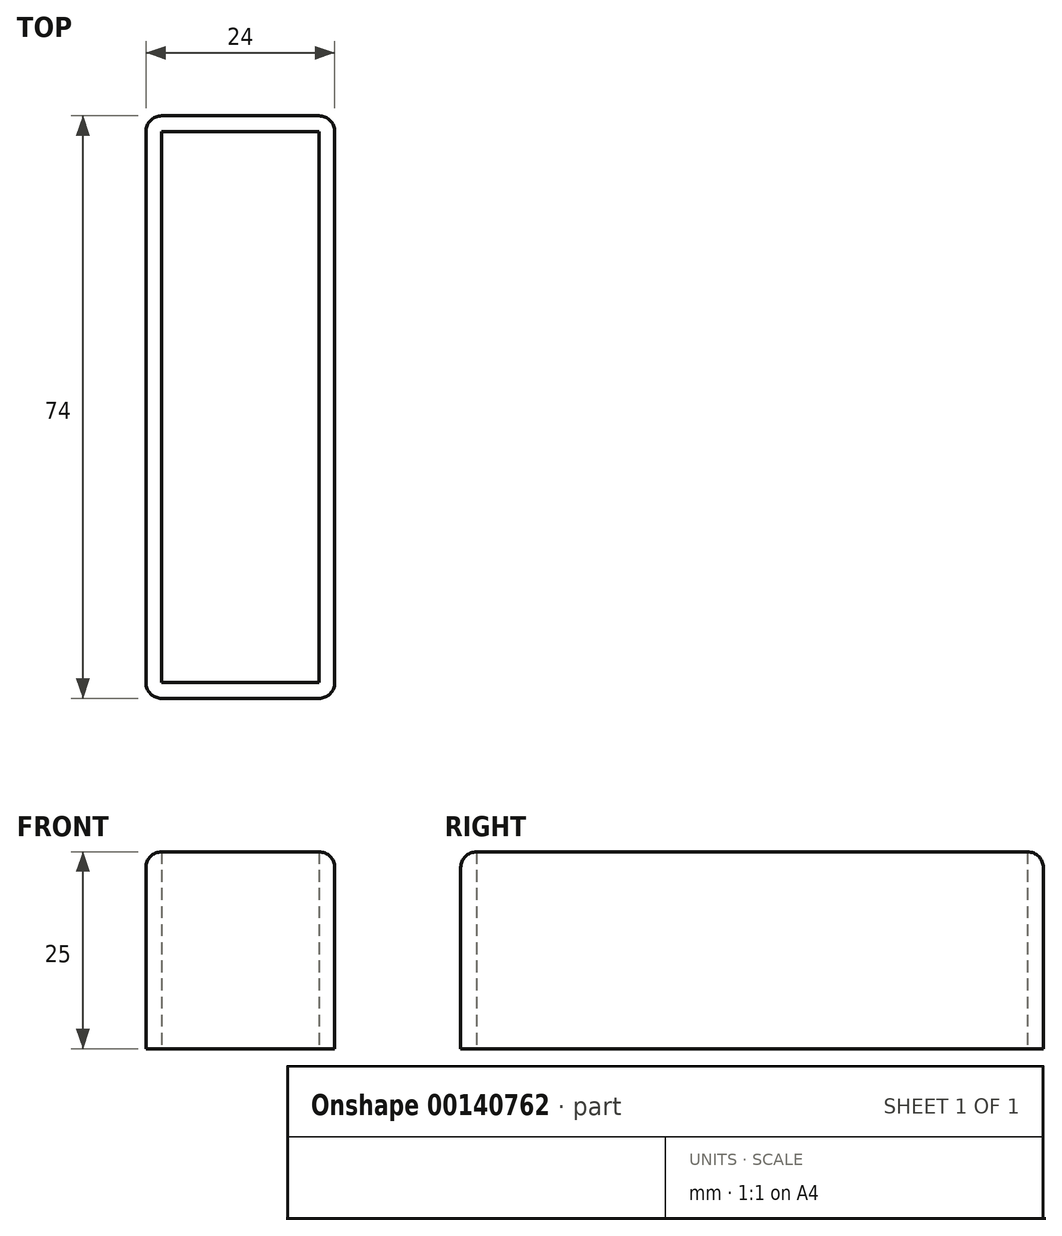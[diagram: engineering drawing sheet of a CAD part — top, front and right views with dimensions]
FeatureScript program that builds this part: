
annotation { "Feature Type Name" : "Feature", "Feature Type Description" : "" }
export const myFeature = defineFeature(function(context is Context, id is Id, definition is map)
    precondition{}
    {
        {
            var Q0;
            Q0=qCreatedBy(makeId("Top.planeOp"),FACE);
            var sketch = newSketch(context, id + "F0", { "sketchPlane" : qUnion([Q0])});
            skLineSegment(sketch, "E0.bottom", {"start": v(10, -35) * mm, "end": v(-10, -35) * mm});
            skLineSegment(sketch, "E0.top", {"start": v(10, 35) * mm, "end": v(-10, 35) * mm});
            skLineSegment(sketch, "E0.left", {"start": v(10, -35) * mm, "end": v(10, 35) * mm});
            skLineSegment(sketch, "E0.right", {"start": v(-10, -35) * mm, "end": v(-10, 35) * mm});
            skPoint(sketch, "E0.middle", {"position": v(0, 0) * mm});
            skLineSegment(sketch, "E1.bottom", {"start": v(12, -37) * mm, "end": v(-12, -37) * mm});
            skLineSegment(sketch, "E1.top", {"start": v(12, 37) * mm, "end": v(-12, 37) * mm});
            skLineSegment(sketch, "E1.left", {"start": v(12, -37) * mm, "end": v(12, 37) * mm});
            skLineSegment(sketch, "E1.right", {"start": v(-12, -37) * mm, "end": v(-12, 37) * mm});
            skSolve(sketch);
        }
        {
            var Q0;
            Q0=makeQuery(id+"F0.imprint","IMPRINT",FACE,{"disambiguationData":[TD([[makeQuery(id+"F0.imprint","IMPRINT",EDGE,{"derivedFrom":sQuery(id+"F0.wireOp",EDGE,"E0.bottom")}),1.0]])]});
            extrude(context, id + "F1", {"entities" : qUnion([Q0]), "depth" : 25 * mm});
        }
        {
            var Q0;
            Q0=makeQuery(id+"F1.opExtrude","SWEPT_EDGE",EDGE,{"disambiguationData":[OSD([sQuery(id+"F0.wireOp",EDGE,"E1.bottom"),sQuery(id+"F0.wireOp",EDGE,"E1.right")])]});
            var Q1;
            Q1=makeQuery(id+"F1.opExtrude","SWEPT_EDGE",EDGE,{"disambiguationData":[OSD([sQuery(id+"F0.wireOp",EDGE,"E1.bottom"),sQuery(id+"F0.wireOp",EDGE,"E1.left")])]});
            var Q2;
            Q2=makeQuery(id+"F1.opExtrude","SWEPT_EDGE",EDGE,{"disambiguationData":[OSD([sQuery(id+"F0.wireOp",EDGE,"E1.top"),sQuery(id+"F0.wireOp",EDGE,"E1.left")])]});
            var Q3;
            Q3=makeQuery(id+"F1.opExtrude","SWEPT_EDGE",EDGE,{"disambiguationData":[OSD([sQuery(id+"F0.wireOp",EDGE,"E1.top"),sQuery(id+"F0.wireOp",EDGE,"E1.right")])]});
            fillet(context, id + "F2", {"entities" : qUnion([Q0, Q1, Q2, Q3]), "radius" : 2 * mm, "tangentPropagation" : true, "allowEdgeOverflow" : false});
        }
        {
            var Q0;
            Q0=makeQuery(id+"F1.opExtrude","CAP_EDGE",EDGE,{"disambiguationData":[OSD([sQuery(id+"F0.wireOp",EDGE,"E1.right")])],"isStart":false});
            fillet(context, id + "F3", {"entities" : qUnion([Q0]), "radius" : 2 * mm, "tangentPropagation" : true, "allowEdgeOverflow" : false});
        }
    });
